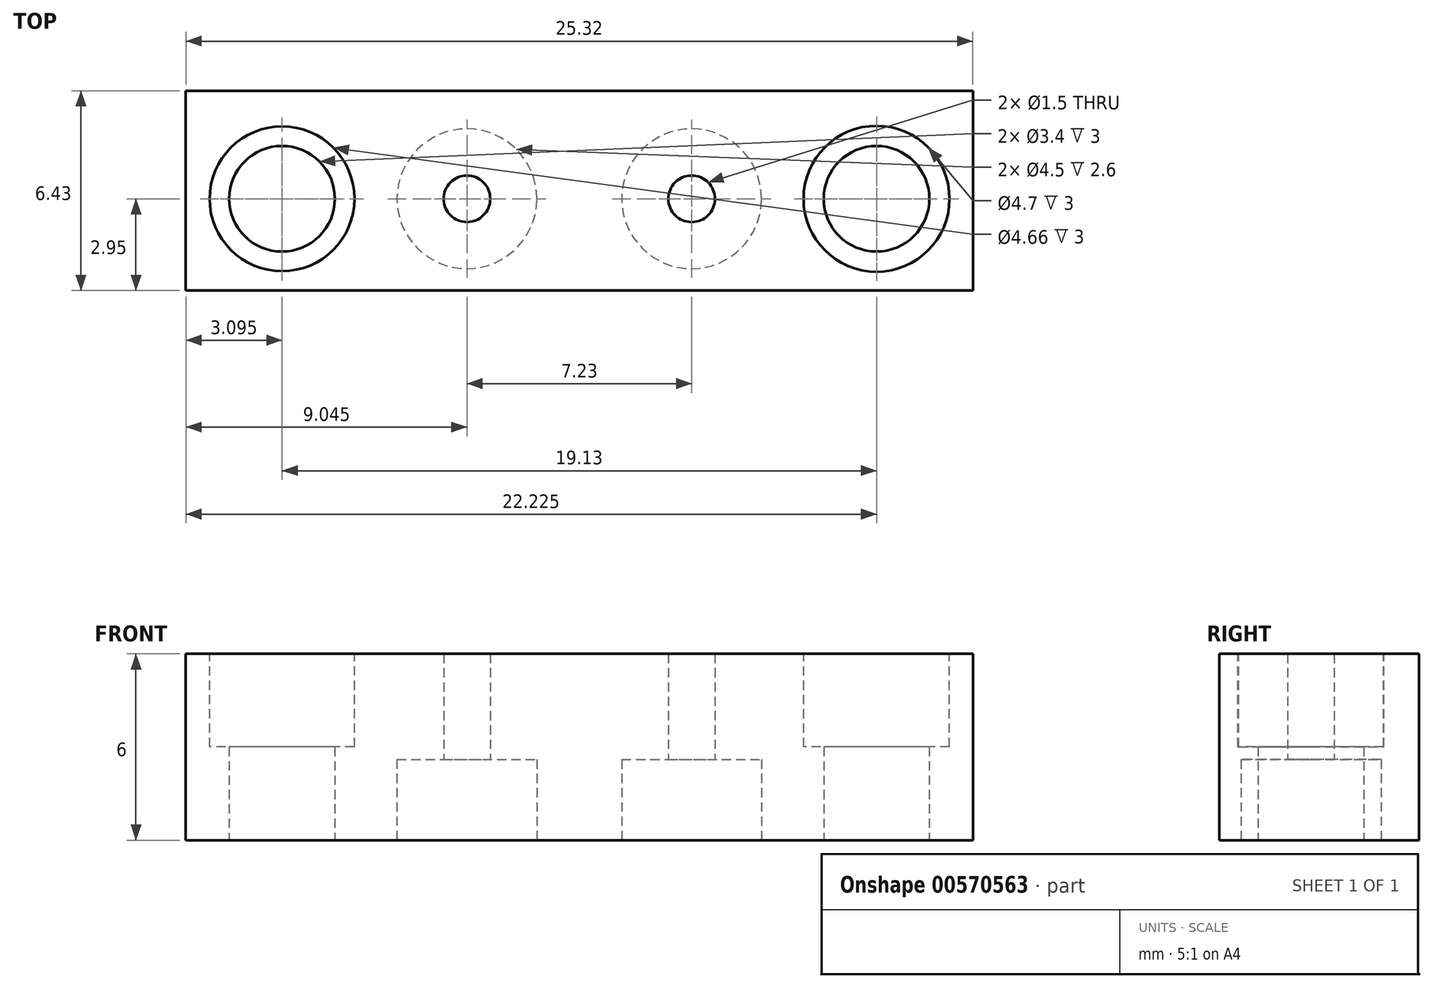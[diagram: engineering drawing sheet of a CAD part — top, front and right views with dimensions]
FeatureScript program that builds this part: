
annotation { "Feature Type Name" : "Feature", "Feature Type Description" : "" }
export const myFeature = defineFeature(function(context is Context, id is Id, definition is map)
    precondition{}
    {
        {
            var Q0;
            Q0=qCreatedBy(makeId("Top.planeOp"),FACE);
            var sketch = newSketch(context, id + "F0", { "sketchPlane" : qUnion([Q0])});
            skLineSegment(sketch, "E0.left", {"start": v(12.66, 3.48) * mm, "end": v(12.66, 0) * mm});
            skLineSegment(sketch, "E0.right", {"start": v(-12.66, 3.48) * mm, "end": v(-12.66, -2.95) * mm});
            skPoint(sketch, "E0.middle", {"position": v(0, 0) * mm});
            skCircle(sketch, "E1", {"center": v(-9.57, 0) * mm, "radius": 1.7 * mm});
            skCircle(sketch, "E2", {"center": v(9.57, 0) * mm, "radius": 1.7 * mm});
            skPoint(sketch, "E3.orphan", {"position": v(-12.66, 0) * mm});
            skPoint(sketch, "E4.orphan", {"position": v(12.66, 0) * mm});
            skCircle(sketch, "E5", {"center": v(-3.62, 0) * mm, "radius": 0.75 * mm});
            skCircle(sketch, "E6", {"center": v(3.62, 0) * mm, "radius": 0.75 * mm});
            skLineSegment(sketch, "E7", {"start": v(-12.66, 3.48) * mm, "end": v(12.66, 3.48) * mm});
            skLineSegment(sketch, "E8", {"start": v(-12.66, -2.95) * mm, "end": v(12.66, -2.95) * mm});
            skLineSegment(sketch, "E9", {"start": v(12.66, 0) * mm, "end": v(12.66, -2.95) * mm});
            skSolve(sketch);
        }
        {
            var Q0;
            Q0=makeQuery(id+"F0.imprint","IMPRINT",FACE,{"disambiguationData":[TD([[makeQuery(id+"F0.imprint","IMPRINT",EDGE,{"derivedFrom":sQuery(id+"F0.wireOp",EDGE,"E0.left")}),-1.0]])]});
            extrude(context, id + "F1", {"entities" : qUnion([Q0]), "depth" : 6 * mm, "offsetDistance" : 25.4 * mm});
        }
        {
            var Q0;
            Q0=makeQuery(id+"F1.opExtrude","CAP_FACE",FACE,{"disambiguationData":[OSD([sQuery(id+"F0.wireOp",EDGE,"E0.left"),sQuery(id+"F0.wireOp",EDGE,"E0.right"),sQuery(id+"F0.wireOp",EDGE,"E1"),sQuery(id+"F0.wireOp",EDGE,"E2"),sQuery(id+"F0.wireOp",EDGE,"E5"),sQuery(id+"F0.wireOp",EDGE,"E6"),sQuery(id+"F0.wireOp",EDGE,"E7"),sQuery(id+"F0.wireOp",EDGE,"E8"),sQuery(id+"F0.wireOp",EDGE,"E9")])],"isStart":false});
            var sketch = newSketch(context, id + "F2", { "sketchPlane" : qUnion([Q0])});
            skCircle(sketch, "E10", {"center": v(-9.57, 0) * mm, "radius": 2.33 * mm});
            skCircle(sketch, "E11", {"center": v(9.57, 0) * mm, "radius": 2.35 * mm});
            skSolve(sketch);
        }
        {
            var Q0;
            Q0=makeQuery(id+"F2.imprint","IMPRINT",FACE,{"disambiguationData":[TD([[makeQuery(id+"F2.imprint","IMPRINT",EDGE,{"derivedFrom":sQuery(id+"F2.wireOp",EDGE,"E10")}),1.0]])]});
            var Q1;
            Q1=makeQuery(id+"F2.imprint","IMPRINT",FACE,{"disambiguationData":[TD([[makeQuery(id+"F2.imprint","IMPRINT",EDGE,{"derivedFrom":sQuery(id+"F2.wireOp",EDGE,"E11")}),1.0]])]});
            extrude(context, id + "F3", {"entities" : qUnion([Q0, Q1]), "operationType" : NewBodyOperationType.REMOVE, "depth" : -3 * mm, "offsetDistance" : 25.4 * mm});
        }
        {
            var Q0;
            Q0=makeQuery(id+"F1.opExtrude","CAP_FACE",FACE,{"disambiguationData":[OSD([sQuery(id+"F0.wireOp",EDGE,"E0.left"),sQuery(id+"F0.wireOp",EDGE,"E0.right"),sQuery(id+"F0.wireOp",EDGE,"E1"),sQuery(id+"F0.wireOp",EDGE,"E2"),sQuery(id+"F0.wireOp",EDGE,"E5"),sQuery(id+"F0.wireOp",EDGE,"E6"),sQuery(id+"F0.wireOp",EDGE,"E7"),sQuery(id+"F0.wireOp",EDGE,"E8"),sQuery(id+"F0.wireOp",EDGE,"E9")])],"isStart":true});
            var sketch = newSketch(context, id + "F4", { "sketchPlane" : qUnion([Q0])});
            skCircle(sketch, "E12", {"center": v(-3.62, 0) * mm, "radius": 2.25 * mm});
            skCircle(sketch, "E13", {"center": v(3.62, 0) * mm, "radius": 2.25 * mm});
            skSolve(sketch);
        }
        {
            var Q0;
            Q0=makeQuery(id+"F4.imprint","IMPRINT",FACE,{"disambiguationData":[TD([[makeQuery(id+"F4.imprint","IMPRINT",EDGE,{"derivedFrom":makeQuery(id+"F1.opExtrude","CAP_EDGE",EDGE,{"disambiguationData":[OSD([sQuery(id+"F0.wireOp",EDGE,"E5")])],"isStart":true})}),-1.0]])]});
            var Q1;
            Q1=makeQuery(id+"F4.imprint","IMPRINT",FACE,{"disambiguationData":[TD([[makeQuery(id+"F4.imprint","IMPRINT",EDGE,{"derivedFrom":makeQuery(id+"F1.opExtrude","CAP_EDGE",EDGE,{"disambiguationData":[OSD([sQuery(id+"F0.wireOp",EDGE,"E6")])],"isStart":true})}),-1.0]])]});
            var Q2;
            Q2=makeQuery(id+"F4.imprint","IMPRINT",FACE,{"disambiguationData":[TD([[makeQuery(id+"F4.imprint","IMPRINT",EDGE,{"derivedFrom":sQuery(id+"F4.wireOp",EDGE,"E13")}),1.0]])]});
            var Q3;
            Q3=makeQuery(id+"F4.imprint","IMPRINT",FACE,{"disambiguationData":[TD([[makeQuery(id+"F4.imprint","IMPRINT",EDGE,{"derivedFrom":sQuery(id+"F4.wireOp",EDGE,"E12")}),1.0]])]});
            extrude(context, id + "F5", {"entities" : qUnion([Q0, Q1, Q2, Q3]), "operationType" : NewBodyOperationType.REMOVE, "oppositeDirection" : true, "depth" : 2.6 * mm, "offsetDistance" : 25.4 * mm});
        }
    });
